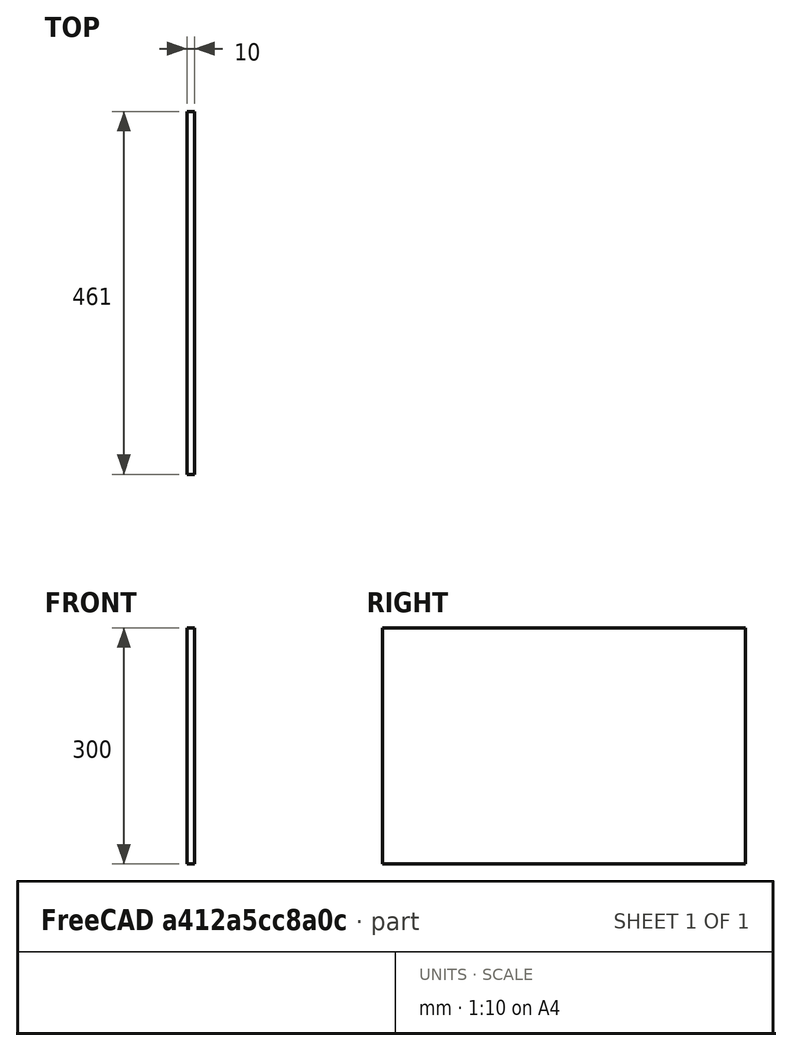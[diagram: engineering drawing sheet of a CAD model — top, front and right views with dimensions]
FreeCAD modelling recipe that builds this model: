
FCSTD DOCUMENT  (FreeCAD 0.18R16131 (Git))
Label: 500_Front_YZ_2
License: All rights reserved
LicenseURL: http://en.wikipedia.org/wiki/All_rights_reserved
objects: Sketcher::SketchObject×1, Spreadsheet::Sheet×1, PartDesign::Pad×1, PartDesign::Body×1
note: 4 computed .brp shape members not serialized (recipe doc carries the construction recipe); baked Part::Feature solids carry a one-line shape summary decoded from their .brp

FEATURE [Sketcher::SketchObject] Sketch
  MapMode = 4
  Placement = pos=(0,0,0) rot=(0.57735,0.57735,0.57735;2.0944rad)
  Support = -> [XY_Plane]
  expr: Constraints[6] = Spreadsheet.nY
  expr: Constraints[5] = Spreadsheet.nZ
  sketch-geometry (5):
    g0: LineSegment StartX=0 StartY=0 StartZ=0 EndX=0 EndY=300 EndZ=0
    g1: LineSegment StartX=461 StartY=0 StartZ=0 EndX=461 EndY=300 EndZ=0
    g2: LineSegment StartX=461 StartY=300 StartZ=0 EndX=0 EndY=300 EndZ=0
    g3: LineSegment StartX=230.5 StartY=0 StartZ=0 EndX=0 EndY=0 EndZ=0
    g4: LineSegment StartX=461 StartY=0 StartZ=0 EndX=230.5 EndY=0 EndZ=0
  constraints (14):
    c: Vertical(g0)
    c: Vertical(g1)
    c: Coincident(g2,g1)
    c: Coincident(g2,g0)
    c: Horizontal(g2)
    c: DistanceY(g1,g1) = 300
    c: DistanceX(g2,g2) = 461
    c: Coincident(g3,g0)
    c: Coincident(g4,g1)
    c: Horizontal(g4)
    c: Equal(g3,g4)
    c: Coincident(g4,g3)
    c: Horizontal(g3)
    c: Coincident(g0,g-1)
FEATURE [Spreadsheet::Sheet] Spreadsheet  label="xls"
  cells = B7=KEYBOARD FRONT; B8=Width; C8=nY; D8(nY)==480 - 19; B9=Height; C9=nZ; D9(nZ)=300; E9=F(T); B10=Thickness; C10=nT; D10(nT)=10
FEATURE [PartDesign::Pad] Pad
  Length = 10
  Length2 = 100
  Profile = -> Sketch
  Reversed = true
  Type = 0
  expr: Length = Spreadsheet.nT
FEATURE [PartDesign::Body] Body
  Group = -> [Sketch,Pad]
  Origin = -> Origin
  Tip = -> Pad
